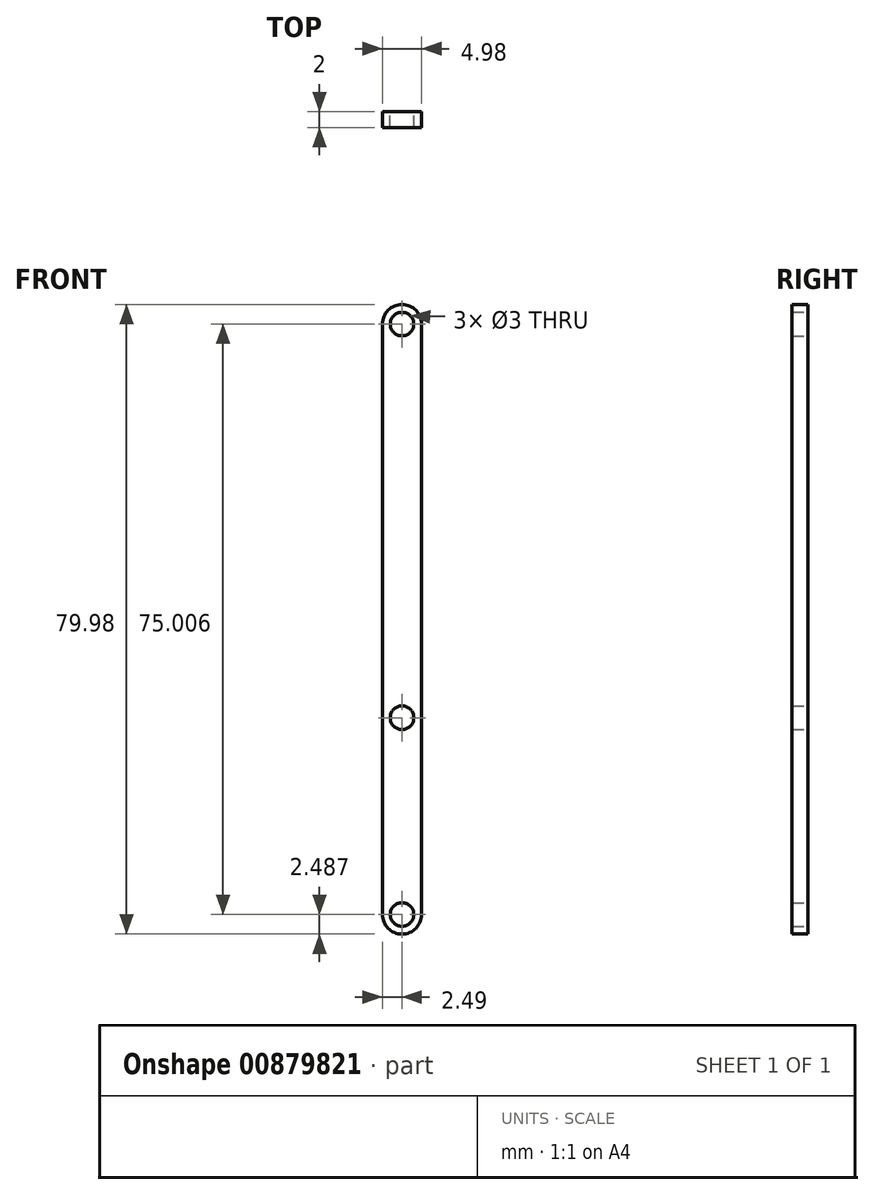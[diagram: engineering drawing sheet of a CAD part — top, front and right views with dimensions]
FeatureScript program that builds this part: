
annotation { "Feature Type Name" : "Feature", "Feature Type Description" : "" }
export const myFeature = defineFeature(function(context is Context, id is Id, definition is map)
    precondition{}
    {
        {
            var Q0;
            Q0=qCreatedBy(makeId("Front.planeOp"),FACE);
            var sketch = newSketch(context, id + "F0", { "sketchPlane" : qUnion([Q0])});
            skLineSegment(sketch, "E0.left", {"start": v(2.49, 37.5) * mm, "end": v(2.49, -37.5) * mm});
            skLineSegment(sketch, "E0.right", {"start": v(-2.49, 37.5) * mm, "end": v(-2.49, -37.5) * mm});
            skPoint(sketch, "E0.middle", {"position": v(0, 0) * mm});
            skArc(sketch, "E1", {"start": v(2.49, 37.5) * mm, "mid": v(0, 40) * mm, "end": v(-2.49, 37.5) * mm});
            skArc(sketch, "E2", {"start": v(-2.49, -37.5) * mm, "mid": v(0, -40) * mm, "end": v(2.49, -37.5) * mm});
            skCircle(sketch, "E3", {"center": v(0, 37.5) * mm, "radius": 1.5 * mm});
            skCircle(sketch, "E4", {"center": v(0, -37.5) * mm, "radius": 1.5 * mm});
            skCircle(sketch, "E5", {"center": v(0, -12.5) * mm, "radius": 1.5 * mm});
            skSolve(sketch);
        }
        {
            var Q0;
            Q0=makeQuery(id+"F0.imprint","IMPRINT",FACE,{"disambiguationData":[TD([[makeQuery(id+"F0.imprint","IMPRINT",EDGE,{"derivedFrom":sQuery(id+"F0.wireOp",EDGE,"E0.left")}),-1.0]])]});
            extrude(context, id + "F1", {"entities" : qUnion([Q0]), "endBound" : BoundingType.SYMMETRIC, "depth" : 2 * mm, "offsetDistance" : 25.4 * mm});
        }
    });
